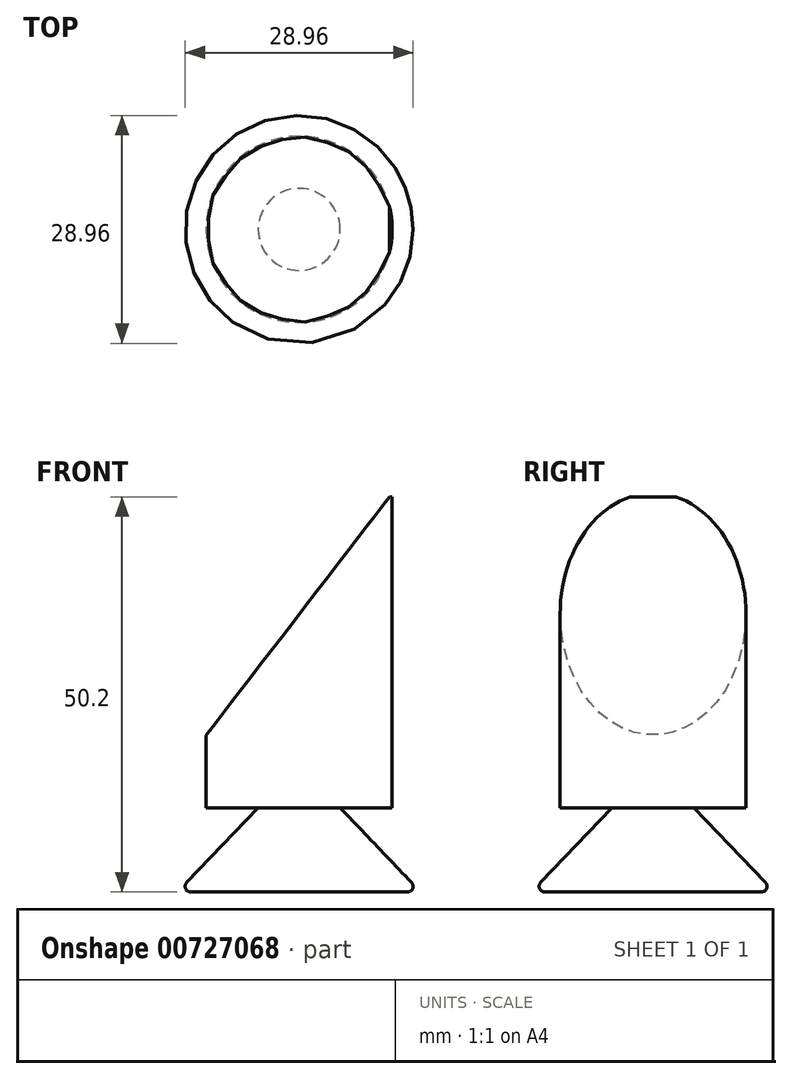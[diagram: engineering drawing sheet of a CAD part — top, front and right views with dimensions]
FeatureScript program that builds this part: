
annotation { "Feature Type Name" : "Feature", "Feature Type Description" : "" }
export const myFeature = defineFeature(function(context is Context, id is Id, definition is map)
    precondition{}
    {
        {
            var Q0;
            Q0=qCreatedBy(makeId("Front.planeOp"),FACE);
            var sketch = newSketch(context, id + "F0", { "sketchPlane" : qUnion([Q0])});
            skLineSegment(sketch, "E0", {"start": v(0, 0) * mm, "end": v(-15.43, 0) * mm});
            skLineSegment(sketch, "E1", {"start": v(-15.43, 0) * mm, "end": v(-5.2, 10.72) * mm});
            skLineSegment(sketch, "E2", {"start": v(-5.2, 10.72) * mm, "end": v(-11.82, 10.72) * mm});
            skLineSegment(sketch, "E3", {"start": v(-11.82, 10.72) * mm, "end": v(-11.82, 50.2) * mm});
            skLineSegment(sketch, "E4", {"start": v(-11.82, 50.2) * mm, "end": v(0, 50.2) * mm});
            skLineSegment(sketch, "E5", {"start": v(0, 50.2) * mm, "end": v(0, 0) * mm});
            skSolve(sketch);
        }
        {
            var Q0;
            Q0 = qSketchRegion(id + "F0", true);
            var Q1;
            Q1=sQuery(id+"F0.wireOp",EDGE,"E5");
            revolve(context, id + "F1", {"surfaceOperationType" : NewSurfaceOperationType.NEW, "entities" : qUnion([Q0]), "axis" : qUnion([Q1]), "revolveType" : RevolveType.FULL});
        }
        {
            var Q0;
            Q0=qCreatedBy(makeId("Front.planeOp"),FACE);
            var sketch = newSketch(context, id + "F2", { "sketchPlane" : qUnion([Q0])});
            skLineSegment(sketch, "E6", {"start": v(14.23, 53.8) * mm, "end": v(-17.03, 13.13) * mm});
            skLineSegment(sketch, "E7", {"start": v(-17.03, 13.13) * mm, "end": v(-17.03, 55.8) * mm});
            skLineSegment(sketch, "E8", {"start": v(-17.03, 55.8) * mm, "end": v(14.23, 53.8) * mm});
            skSolve(sketch);
        }
        {
            var Q0;
            Q0 = qSketchRegion(id + "F2", true);
            extrude(context, id + "F3", {"entities" : qUnion([Q0]), "operationType" : NewBodyOperationType.REMOVE, "endBound" : BoundingType.SYMMETRIC, "oppositeDirection" : true, "depth" : 37.4 * mm, "offsetDistance" : 25 * mm});
        }
        {
            var Q0;
            Q0=makeQuery(id+"F1.opRevolve","SWEPT_EDGE",EDGE,{"disambiguationData":[OSD([sQuery(id+"F0.wireOp",EDGE,"E0"),sQuery(id+"F0.wireOp",EDGE,"E1")])]});
            fillet(context, id + "F4", {"entities" : qUnion([Q0]), "radius" : 0.71 * mm, "tangentPropagation" : true, "allowEdgeOverflow" : false});
        }
    });
